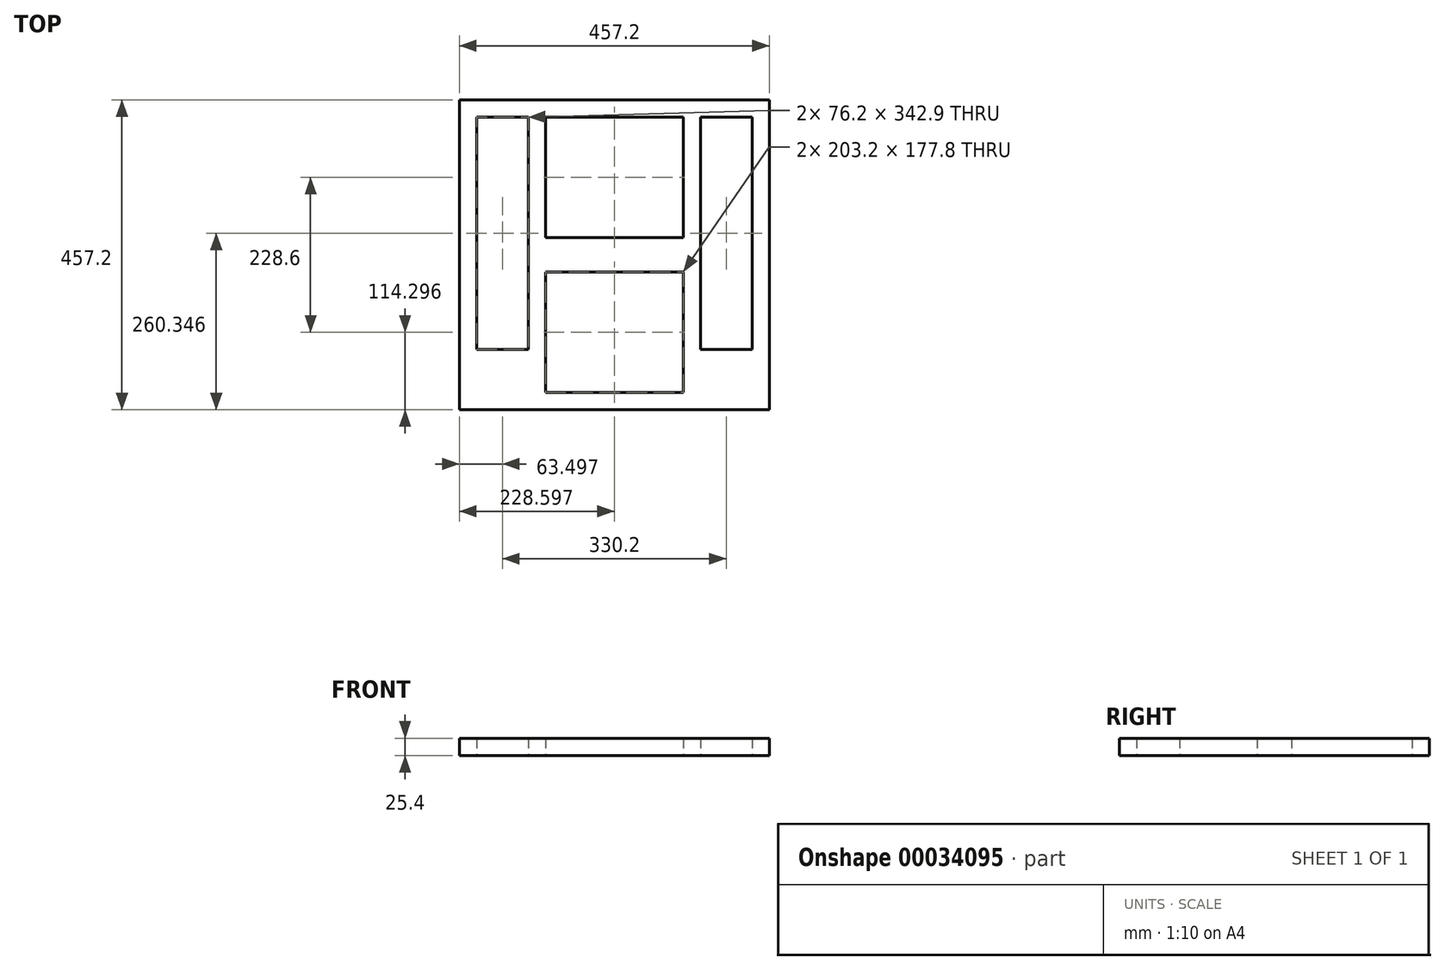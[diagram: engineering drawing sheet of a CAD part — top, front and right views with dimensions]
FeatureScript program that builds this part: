
annotation { "Feature Type Name" : "Feature", "Feature Type Description" : "" }
export const myFeature = defineFeature(function(context is Context, id is Id, definition is map)
    precondition{}
    {
        {
            var Q0;
            Q0=qCreatedBy(makeId("Top.planeOp"),FACE);
            var sketch = newSketch(context, id + "F0", { "sketchPlane" : qUnion([Q0])});
            skLineSegment(sketch, "E0.bottom", {"start": v(-391.6, 125.29) * mm, "end": v(65.6, 125.29) * mm});
            skLineSegment(sketch, "E0.top", {"start": v(-391.6, -331.91) * mm, "end": v(65.6, -331.91) * mm});
            skLineSegment(sketch, "E0.left", {"start": v(-391.6, 125.29) * mm, "end": v(-391.6, -331.91) * mm});
            skLineSegment(sketch, "E0.right", {"start": v(65.6, 125.29) * mm, "end": v(65.6, -331.91) * mm});
            skLineSegment(sketch, "E1", {"start": v(-264.6, 99.89) * mm, "end": v(-264.6, -306.51) * mm});
            skLineSegment(sketch, "E2", {"start": v(-61.4, 99.89) * mm, "end": v(-61.4, -306.51) * mm});
            skLineSegment(sketch, "E3", {"start": v(-61.4, -128.71) * mm, "end": v(-264.6, -128.71) * mm});
            skLineSegment(sketch, "E4", {"start": v(-264.6, -77.91) * mm, "end": v(-61.4, -77.91) * mm});
            skLineSegment(sketch, "E5", {"start": v(-366.2, 99.89) * mm, "end": v(40.2, 99.89) * mm});
            skLineSegment(sketch, "E6", {"start": v(40.2, 99.89) * mm, "end": v(40.2, -306.51) * mm});
            skLineSegment(sketch, "E7", {"start": v(40.2, -306.51) * mm, "end": v(-366.2, -306.51) * mm});
            skLineSegment(sketch, "E8", {"start": v(-366.2, -306.51) * mm, "end": v(-366.2, 99.89) * mm});
            skLineSegment(sketch, "E9", {"start": v(-290, 99.89) * mm, "end": v(-290, -306.51) * mm});
            skLineSegment(sketch, "E10", {"start": v(-36, 99.89) * mm, "end": v(-36, -306.51) * mm});
            skLineSegment(sketch, "E11", {"start": v(-264.6, -103.31) * mm, "end": v(-61.4, -103.31) * mm});
            skLineSegment(sketch, "E12", {"start": v(-61.4, -103.31) * mm, "end": v(-264.6, -103.31) * mm});
            skPoint(sketch, "E13.orphan", {"position": v(-264.6, -331.91) * mm});
            skLineSegment(sketch, "E14", {"start": v(-366.2, -243.01) * mm, "end": v(-290, -243.01) * mm});
            skLineSegment(sketch, "E15", {"start": v(-366.2, -103.31) * mm, "end": v(-290, -103.31) * mm});
            skLineSegment(sketch, "E16", {"start": v(-36, -243.01) * mm, "end": v(40.2, -243.01) * mm});
            skLineSegment(sketch, "E17", {"start": v(-36, -103.31) * mm, "end": v(40.2, -103.31) * mm});
            skSolve(sketch);
        }
        {
            var Q0;
            Q0=makeQuery(id+"F0.imprint","IMPRINT",FACE,{"disambiguationData":[TD([[makeQuery(id+"F0.imprint","IMPRINT",EDGE,{"derivedFrom":sQuery(id+"F0.wireOp",EDGE,"E0.bottom")}),-1.0]])]});
            extrude(context, id + "F1", {"entities" : qUnion([Q0]), "depth" : 25.4 * mm});
        }
        {
            var Q0;
            {var subQ0=sQuery(id+"F0.wireOp",EDGE,"E9");Q0=makeQuery(id+"F0.imprint","IMPRINT",FACE,{"disambiguationData":[TD([[makeQuery(id+"F0.imprint","IMPRINT",EDGE,{"derivedFrom":subQ0}),1.0]])]});}
            var Q1;
            {var subQ0=sQuery(id+"F0.wireOp",EDGE,"E10");Q1=makeQuery(id+"F0.imprint","IMPRINT",FACE,{"disambiguationData":[TD([[makeQuery(id+"F0.imprint","IMPRINT",EDGE,{"derivedFrom":subQ0}),-1.0]])]});}
            var Q2;
            {var subQ1=sQuery(id+"F0.wireOp",EDGE,"E3");Q2=makeQuery(id+"F0.imprint","IMPRINT",FACE,{"disambiguationData":[TD([[makeQuery(id+"F0.imprint","IMPRINT",EDGE,{"derivedFrom":subQ1}),-1.0]])]});}
            var Q3;
            {var subQ1=sQuery(id+"F0.wireOp",EDGE,"E4");Q3=makeQuery(id+"F0.imprint","IMPRINT",FACE,{"disambiguationData":[TD([[makeQuery(id+"F0.imprint","IMPRINT",EDGE,{"derivedFrom":subQ1}),-1.0]])]});}
            extrude(context, id + "F2", {"entities" : qUnion([Q0, Q1, Q2, Q3]), "operationType" : NewBodyOperationType.ADD, "depth" : 25.4 * mm});
        }
        {
            var Q0;
            {var subQ1=sQuery(id+"F0.wireOp",EDGE,"E14");Q0=makeQuery(id+"F0.imprint","IMPRINT",FACE,{"disambiguationData":[TD([[makeQuery(id+"F0.imprint","IMPRINT",EDGE,{"derivedFrom":subQ1}),-1.0]])]});}
            var Q1;
            {var subQ1=sQuery(id+"F0.wireOp",EDGE,"E16");Q1=makeQuery(id+"F0.imprint","IMPRINT",FACE,{"disambiguationData":[TD([[makeQuery(id+"F0.imprint","IMPRINT",EDGE,{"derivedFrom":subQ1}),-1.0]])]});}
            extrude(context, id + "F3", {"entities" : qUnion([Q0, Q1]), "operationType" : NewBodyOperationType.ADD, "depth" : 25.4 * mm});
        }
    });
